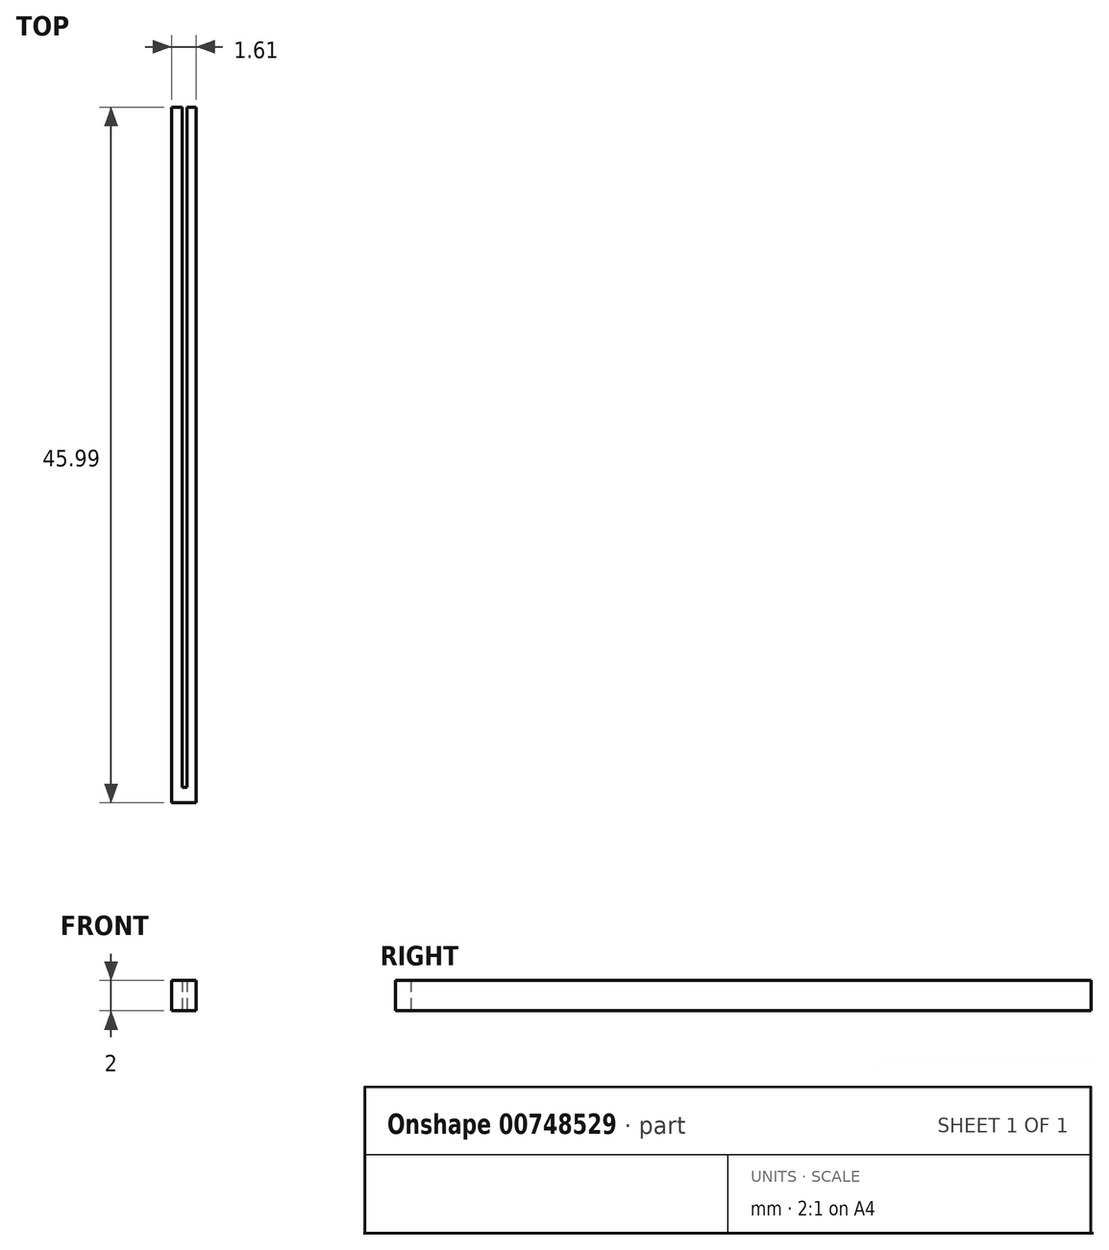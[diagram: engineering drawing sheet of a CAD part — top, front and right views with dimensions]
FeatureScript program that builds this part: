
annotation { "Feature Type Name" : "Feature", "Feature Type Description" : "" }
export const myFeature = defineFeature(function(context is Context, id is Id, definition is map)
    precondition{}
    {
        {
            var Q0;
            Q0=qCreatedBy(makeId("Top.planeOp"),FACE);
            var sketch = newSketch(context, id + "F0", { "sketchPlane" : qUnion([Q0])});
            skLineSegment(sketch, "E0.bottom", {"start": v(-41.08, 44.98) * mm, "end": v(-40.38, 44.98) * mm});
            skLineSegment(sketch, "E0.top", {"start": v(-41.08, 0) * mm, "end": v(-40.38, 0) * mm});
            skLineSegment(sketch, "E0.left", {"start": v(-41.08, 44.98) * mm, "end": v(-41.08, 0) * mm});
            skLineSegment(sketch, "E0.right", {"start": v(-40.38, 44.98) * mm, "end": v(-40.38, 0) * mm});
            skLineSegment(sketch, "E1.bottom", {"start": v(-40.05, 44.98) * mm, "end": v(-39.47, 44.98) * mm});
            skLineSegment(sketch, "E1.top", {"start": v(-40.05, 0) * mm, "end": v(-39.47, 0) * mm});
            skLineSegment(sketch, "E1.left", {"start": v(-40.05, 44.98) * mm, "end": v(-40.05, 0) * mm});
            skLineSegment(sketch, "E1.right", {"start": v(-39.47, 44.98) * mm, "end": v(-39.47, 0) * mm});
            skPoint(sketch, "E2.oppositeSnap0", {"position": v(-39.47, 22.49) * mm});
            skLineSegment(sketch, "E2.bottom", {"start": v(-41.08, 0) * mm, "end": v(-39.47, 0) * mm});
            skLineSegment(sketch, "E2.top", {"start": v(-41.08, -1) * mm, "end": v(-39.47, -1) * mm});
            skLineSegment(sketch, "E2.left", {"start": v(-41.08, 0) * mm, "end": v(-41.08, -1) * mm});
            skLineSegment(sketch, "E2.right", {"start": v(-39.47, 0) * mm, "end": v(-39.47, -1) * mm});
            skSolve(sketch);
        }
        {
            var Q0;
            Q0=makeQuery(id+"F0.imprint","IMPRINT",FACE,{"disambiguationData":[TD([[makeQuery(id+"F0.imprint","IMPRINT",EDGE,{"derivedFrom":sQuery(id+"F0.wireOp",EDGE,"E0.bottom")}),-1.0]])]});
            var Q1;
            Q1=makeQuery(id+"F0.imprint","IMPRINT",FACE,{"disambiguationData":[TD([[makeQuery(id+"F0.imprint","IMPRINT",EDGE,{"derivedFrom":sQuery(id+"F0.wireOp",EDGE,"E1.bottom")}),-1.0]])]});
            var Q2;
            Q2=makeQuery(id+"F0.imprint","IMPRINT",FACE,{"disambiguationData":[TD([[makeQuery(id+"F0.imprint","IMPRINT",EDGE,{"derivedFrom":sQuery(id+"F0.wireOp",EDGE,"E2.top")}),1.0]])]});
            extrude(context, id + "F1", {"entities" : qUnion([Q0, Q1, Q2]), "depth" : 2 * mm, "offsetDistance" : 25.4 * mm});
        }
    });
